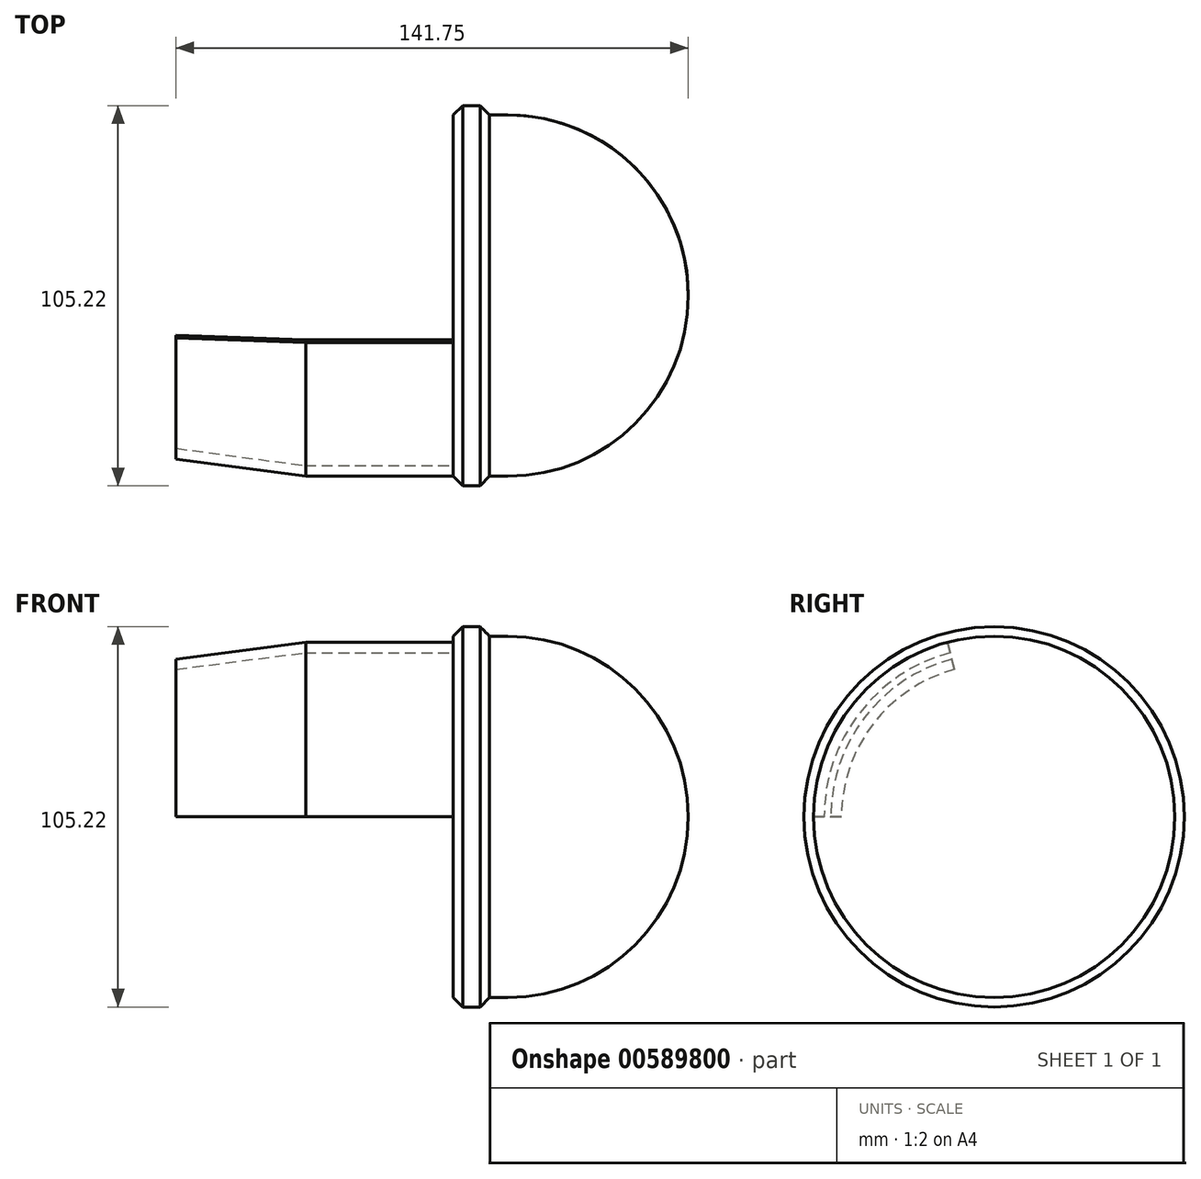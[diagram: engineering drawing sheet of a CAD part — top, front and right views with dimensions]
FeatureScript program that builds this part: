
annotation { "Feature Type Name" : "Feature", "Feature Type Description" : "" }
export const myFeature = defineFeature(function(context is Context, id is Id, definition is map)
    precondition{}
    {
        {
            var Q0;
            Q0=qCreatedBy(makeId("Top.planeOp"),FACE);
            var sketch = newSketch(context, id + "F0", { "sketchPlane" : qUnion([Q0])});
            skLineSegment(sketch, "E0", {"start": v(0, 0) * mm, "end": v(0, 50) * mm});
            skLineSegment(sketch, "E1", {"start": v(0, 0) * mm, "end": v(0, -50) * mm});
            skLineSegment(sketch, "E2", {"start": v(0, -50) * mm, "end": v(5, -50) * mm});
            skLineSegment(sketch, "E3", {"start": v(0, 50) * mm, "end": v(5, 50) * mm});
            skLineSegment(sketch, "E4", {"start": v(55, 0) * mm, "end": v(55, 0) * mm});
            skPoint(sketch, "E5.visualSharp", {"position": v(55, 50) * mm});
            skArc(sketch, "E5.filletArc", {"start": v(55, 0) * mm, "mid": v(40.36, 35.36) * mm, "end": v(5, 50) * mm});
            skPoint(sketch, "E6.visualSharp", {"position": v(55, -50) * mm});
            skArc(sketch, "E6.filletArc", {"start": v(5, -50) * mm, "mid": v(40.36, -35.36) * mm, "end": v(55, 0) * mm});
            skLineSegment(sketch, "E7", {"start": v(0, 50) * mm, "end": v(-10, 50) * mm});
            skLineSegment(sketch, "E8", {"start": v(0, -50) * mm, "end": v(-10, -50) * mm});
            skLineSegment(sketch, "E9", {"start": v(-10, 50) * mm, "end": v(-10, -50) * mm});
            skLineSegment(sketch, "E10", {"start": v(-10, 50) * mm, "end": v(-7.4, 52.6) * mm});
            skLineSegment(sketch, "E11", {"start": v(-7.4, 52.6) * mm, "end": v(-2.6, 52.6) * mm});
            skLineSegment(sketch, "E12", {"start": v(-2.6, 52.6) * mm, "end": v(0, 50) * mm});
            skLineSegment(sketch, "E13", {"start": v(0, 0) * mm, "end": v(55, 0) * mm});
            skLineSegment(sketch, "E14", {"start": v(0, 0) * mm, "end": v(-10, 0) * mm});
            skLineSegment(sketch, "E15", {"start": v(-10, -50) * mm, "end": v(-50.86, -50) * mm});
            skLineSegment(sketch, "E16", {"start": v(-50.86, -50) * mm, "end": v(-86.75, -45.2) * mm});
            skLineSegment(sketch, "E17", {"start": v(-86.75, -45.2) * mm, "end": v(-86.75, -42.24) * mm});
            skLineSegment(sketch, "E18", {"start": v(-86.75, -42.24) * mm, "end": v(-51.02, -47.03) * mm});
            skLineSegment(sketch, "E19", {"start": v(-51.02, -47.03) * mm, "end": v(-10, -47.03) * mm});
            skSolve(sketch);
        }
        {
            var Q0;
            Q0=makeQuery(id+"F0.imprint","IMPRINT",FACE,{"disambiguationData":[TD([[makeQuery(id+"F0.imprint","IMPRINT",EDGE,{"derivedFrom":sQuery(id+"F0.wireOp",EDGE,"E0")}),1.0]])]});
            var Q1;
            Q1=makeQuery(id+"F0.imprint","IMPRINT",FACE,{"disambiguationData":[TD([[makeQuery(id+"F0.imprint","IMPRINT",EDGE,{"derivedFrom":sQuery(id+"F0.wireOp",EDGE,"E0")}),-1.0]])]});
            var Q2;
            Q2=makeQuery(id+"F0.imprint","IMPRINT",FACE,{"disambiguationData":[TD([[makeQuery(id+"F0.imprint","IMPRINT",EDGE,{"derivedFrom":sQuery(id+"F0.wireOp",EDGE,"E7")}),-1.0]])]});
            var Q3;
            Q3=sQuery(id+"F0.wireOp",EDGE,"E13");
            revolve(context, id + "F1", {"entities" : qUnion([Q0, Q1, Q2]), "axis" : qUnion([Q3]), "revolveType" : RevolveType.FULL});
        }
        {
            var Q0;
            {var subQ0=sQuery(id+"F0.wireOp",EDGE,"E15");Q0=makeQuery(id+"F0.imprint","IMPRINT",FACE,{"disambiguationData":[TD([[makeQuery(id+"F0.imprint","IMPRINT",EDGE,{"derivedFrom":subQ0}),-1.0]])]});}
            var Q1;
            Q1=sQuery(id+"F0.wireOp",EDGE,"E13");
            revolve(context, id + "F2", {"operationType" : NewBodyOperationType.ADD, "entities" : qUnion([Q0]), "axis" : qUnion([Q1]), "revolveType" : RevolveType.ONE_DIRECTION, "oppositeDirection" : true, "angle" : 75 * degree});
        }
    });
